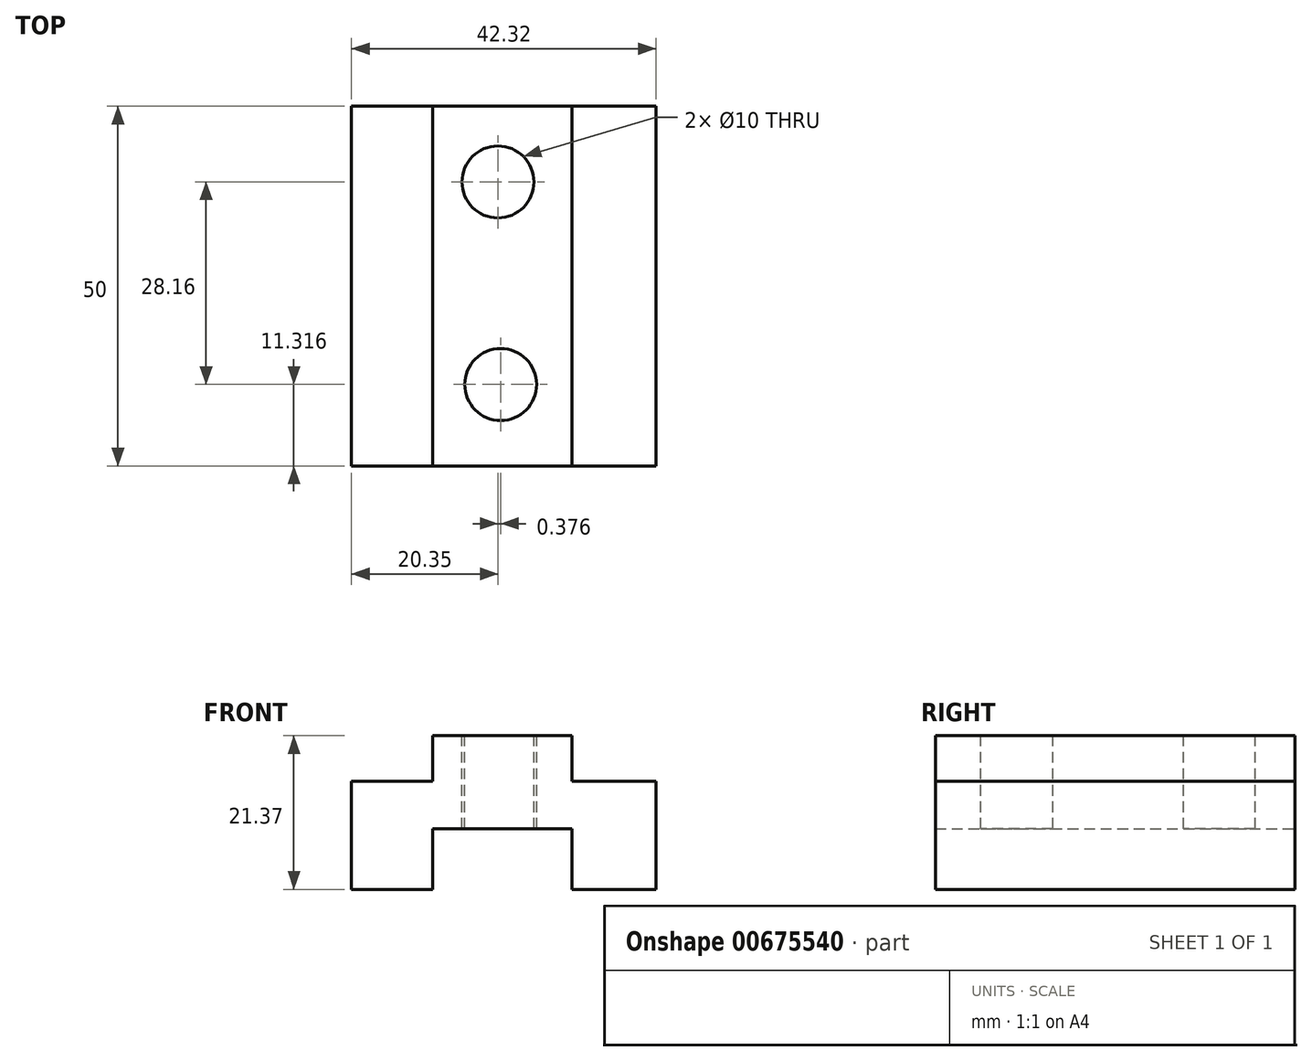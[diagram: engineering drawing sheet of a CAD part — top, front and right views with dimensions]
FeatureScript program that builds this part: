
annotation { "Feature Type Name" : "Feature", "Feature Type Description" : "" }
export const myFeature = defineFeature(function(context is Context, id is Id, definition is map)
    precondition{}
    {
        {
            var Q0;
            Q0=qCreatedBy(makeId("Front.planeOp"),FACE);
            var sketch = newSketch(context, id + "F0", { "sketchPlane" : qUnion([Q0])});
            skLineSegment(sketch, "E0", {"start": v(-45.58, 15.32) * mm, "end": v(-34.28, 15.32) * mm});
            skLineSegment(sketch, "E1", {"start": v(-34.28, 15.32) * mm, "end": v(-34.28, 23.75) * mm});
            skLineSegment(sketch, "E2", {"start": v(-34.28, 23.75) * mm, "end": v(-14.97, 23.75) * mm});
            skLineSegment(sketch, "E3", {"start": v(-14.97, 23.75) * mm, "end": v(-14.97, 15.32) * mm});
            skLineSegment(sketch, "E4", {"start": v(-14.97, 15.32) * mm, "end": v(-3.26, 15.32) * mm});
            skLineSegment(sketch, "E5", {"start": v(-3.26, 15.32) * mm, "end": v(-3.26, 30.32) * mm});
            skLineSegment(sketch, "E6", {"start": v(-3.26, 30.32) * mm, "end": v(-14.97, 30.32) * mm});
            skLineSegment(sketch, "E7", {"start": v(-14.97, 30.32) * mm, "end": v(-14.97, 36.7) * mm});
            skLineSegment(sketch, "E8", {"start": v(-14.97, 36.7) * mm, "end": v(-34.28, 36.7) * mm});
            skLineSegment(sketch, "E9", {"start": v(-34.28, 36.7) * mm, "end": v(-34.28, 30.32) * mm});
            skLineSegment(sketch, "E10", {"start": v(-34.28, 30.32) * mm, "end": v(-45.58, 30.32) * mm});
            skLineSegment(sketch, "E11", {"start": v(-45.58, 30.32) * mm, "end": v(-45.58, 15.32) * mm});
            skSolve(sketch);
        }
        {
            var Q0;
            Q0 = qSketchRegion(id + "F0", true);
            extrude(context, id + "F1", {"entities" : qUnion([Q0]), "depth" : 50 * mm, "offsetDistance" : 25 * mm});
        }
        {
            var Q0;
            Q0=makeQuery(id+"F1.opExtrude","SWEPT_FACE",FACE,{"disambiguationData":[OSD([sQuery(id+"F0.wireOp",EDGE,"E8")])]});
            var sketch = newSketch(context, id + "F2", { "sketchPlane" : qUnion([Q0])});
            skPoint(sketch, "E12", {"position": v(-25.23, -10.52) * mm});
            skPoint(sketch, "E13", {"position": v(-24.85, -38.68) * mm});
            skSolve(sketch);
        }
        {
            var Q0;
            Q0=sQuery(id+"F2.wireOp",VERTEX,"E12");
            var Q1;
            Q1=makeQuery(id+"F1.opExtrude","SWEPT_BODY",BODY,{"disambiguationData":[OSD([sQuery(id+"F0.wireOp",EDGE,"E0"),sQuery(id+"F0.wireOp",EDGE,"E1"),sQuery(id+"F0.wireOp",EDGE,"E2"),sQuery(id+"F0.wireOp",EDGE,"E3"),sQuery(id+"F0.wireOp",EDGE,"E4"),sQuery(id+"F0.wireOp",EDGE,"E5"),sQuery(id+"F0.wireOp",EDGE,"E6"),sQuery(id+"F0.wireOp",EDGE,"E7"),sQuery(id+"F0.wireOp",EDGE,"E8"),sQuery(id+"F0.wireOp",EDGE,"E9"),sQuery(id+"F0.wireOp",EDGE,"E10"),sQuery(id+"F0.wireOp",EDGE,"E11")])]});
            hole(context, id + "F3", {"style" : HoleStyle.SIMPLE, "endStyle" : HoleEndStyle.THROUGH, "holeDiameter" : 10 * mm, "majorDiameter" : 5 * mm, "isTappedThrough" : true, "tappedDepth" : 12 * mm, "tapClearance" : 3, "locations" : qUnion([Q0]), "scope" : qUnion([Q1])});
        }
        {
            var Q0;
            Q0=sQuery(id+"F2.wireOp",VERTEX,"E13");
            var Q1;
            Q1=makeQuery(id+"F1.opExtrude","SWEPT_BODY",BODY,{"disambiguationData":[OSD([sQuery(id+"F0.wireOp",EDGE,"E0"),sQuery(id+"F0.wireOp",EDGE,"E1"),sQuery(id+"F0.wireOp",EDGE,"E2"),sQuery(id+"F0.wireOp",EDGE,"E3"),sQuery(id+"F0.wireOp",EDGE,"E4"),sQuery(id+"F0.wireOp",EDGE,"E5"),sQuery(id+"F0.wireOp",EDGE,"E6"),sQuery(id+"F0.wireOp",EDGE,"E7"),sQuery(id+"F0.wireOp",EDGE,"E8"),sQuery(id+"F0.wireOp",EDGE,"E9"),sQuery(id+"F0.wireOp",EDGE,"E10"),sQuery(id+"F0.wireOp",EDGE,"E11")])]});
            hole(context, id + "F4", {"style" : HoleStyle.SIMPLE, "endStyle" : HoleEndStyle.THROUGH, "holeDiameter" : 10 * mm, "majorDiameter" : 5 * mm, "isTappedThrough" : true, "tappedDepth" : 12 * mm, "tapClearance" : 3, "locations" : qUnion([Q0]), "scope" : qUnion([Q1])});
        }
    });
